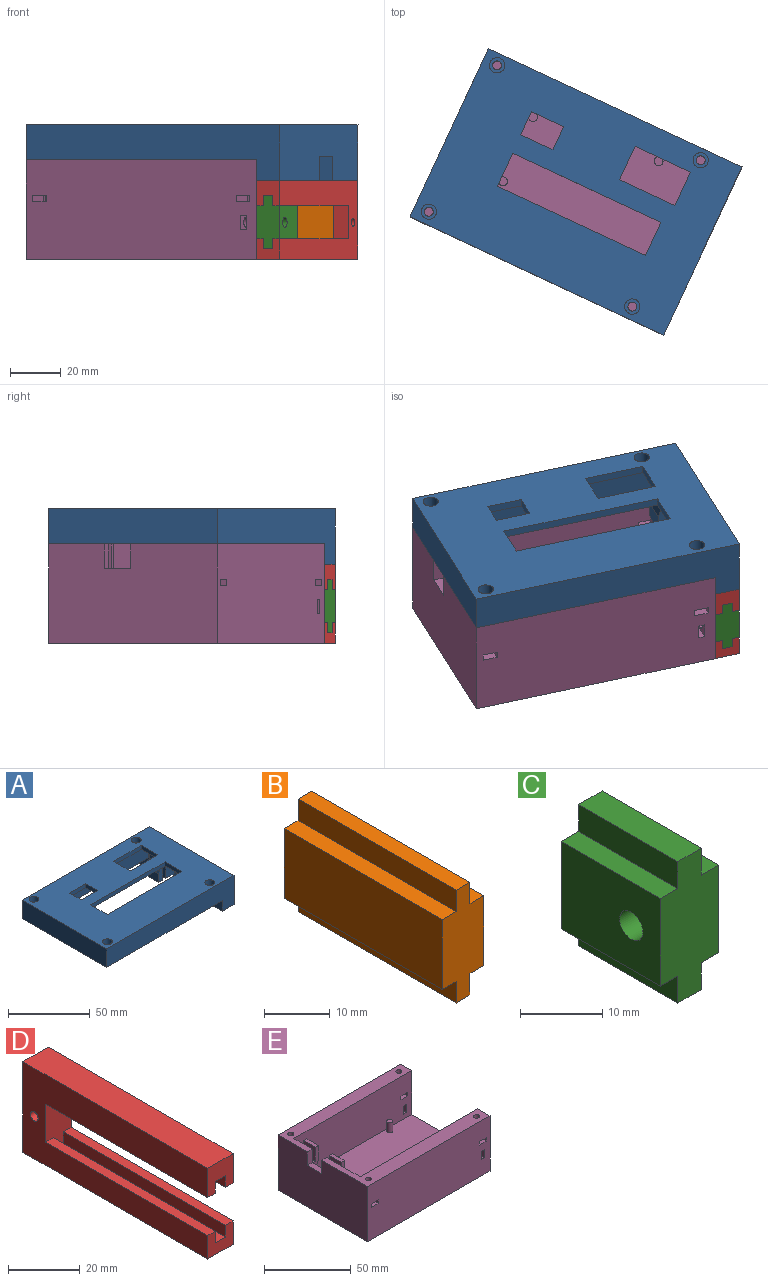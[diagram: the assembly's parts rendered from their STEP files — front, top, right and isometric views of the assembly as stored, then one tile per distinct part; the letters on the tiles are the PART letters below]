
ASSEMBLY  parts=5 mates=8
PART A: 56 faces, bbox 110x73x21.8 mm
  f0: plane 84x54mm, normal (0,0,-1), area 3044.5mm2, adj f1,f13,f14,f15,f25,f26,f27,f28
  f1: plane 73x18.8mm, normal (-1,0,0), area 881mm2, adj f0,f2,f8,f10,f12,f14,f15,f16
  f2: plane 37.4x10mm, normal (0,0,-1), area 374mm2, adj f1,f10,f11,f37
  f3: plane 110x73mm, normal (0,0,1), area 6505.4mm2, adj f9,f10,f11,f12,f18,f20,f22,f24
  f4: cylinder r=1.75mm len=8.8mm, axis (0,0,1), area 96.8mm2, adj f8,f23
  f5: cylinder r=1.75mm len=8.8mm, axis (0,0,1), area 96.8mm2, adj f8,f21
  f6: cylinder r=1.75mm len=8.8mm, axis (0,0,1), area 96.8mm2, adj f8,f19
  f7: cylinder r=1.75mm len=8.8mm, axis (0,0,1), area 96.8mm2, adj f8,f17
  f8: plane 100x73mm, normal (0,0,-1), area 2725.5mm2, adj f1,f4,f5,f6,f7,f9,f10,f12
  f9: plane 73x13.8mm, normal (-1,0,0), area 1007.4mm2, adj f3,f8,f10,f12
  f10: plane 110x21.8mm, normal (0,-1,0), area 1598mm2, adj f1,f2,f3,f8,f9,f11
  f11: plane 73x21.8mm, normal (1,0,0), area 1481.2mm2, adj f2,f3,f10,f12,f16,f37,f38,f39
  f12: plane 110x21.8mm, normal (0,1,0), area 1598mm2, adj f1,f3,f8,f9,f11,f16
  f13: plane 54x10.8mm, normal (1,0,0), area 583.2mm2, adj f0,f8,f14,f15
  f14: plane 84x10.8mm, normal (0,-1,0), area 907.2mm2, adj f0,f1,f8,f13
  f15: plane 84x10.8mm, normal (0,1,0), area 907.2mm2, adj f0,f1,f8,f13
  f16: plane 24x10mm, normal (0,0,-1), area 240mm2, adj f1,f11,f12,f38
  f17: plane 6x6mm, normal (0,0,1), area 18.7mm2, adj f7,f18
  f18: cylinder r=3mm len=6mm, axis (0,0,1), area 94.2mm2, adj f3,f17
  f19: plane 6x6mm, normal (0,0,1), area 18.7mm2, adj f6,f20
  f20: cylinder r=3mm len=6mm, axis (0,0,1), area 94.2mm2, adj f3,f19
  f21: plane 6x6mm, normal (0,0,1), area 18.7mm2, adj f5,f22
  f22: cylinder r=3mm len=6mm, axis (0,0,1), area 94.2mm2, adj f3,f21
  f23: plane 6x6mm, normal (0,0,1), area 18.7mm2, adj f4,f24
  f24: cylinder r=3mm len=6mm, axis (0,0,1), area 94.2mm2, adj f3,f23
  f25: plane 14x3mm, normal (0,-1,0), area 42mm2, adj f0,f3,f26,f28
  f26: plane 10x3mm, normal (1,0,0), area 30mm2, adj f0,f3,f25,f27
  f27: plane 14x3mm, normal (0,1,0), area 42mm2, adj f0,f3,f26,f28
  f28: plane 10x3mm, normal (-1,0,0), area 30mm2, adj f0,f3,f25,f27
  f29: plane 24x3mm, normal (0,-1,0), area 72mm2, adj f0,f3,f30,f32
  f30: plane 14.4x3mm, normal (1,0,0), area 43.2mm2, adj f0,f3,f29,f31
  f31: plane 24x3mm, normal (0,1,0), area 72mm2, adj f0,f3,f30,f32
  f32: plane 14.4x3mm, normal (-1,0,0), area 43.2mm2, adj f0,f3,f29,f31
  f33: plane 14.4x3mm, normal (1,0,0), area 43.2mm2, adj f0,f3,f34,f36
  f34: plane 64.3x3mm, normal (0,1,0), area 192.9mm2, adj f0,f3,f33,f35
  f35: plane 14.4x3mm, normal (-1,0,0), area 43.2mm2, adj f0,f3,f34,f36
  f36: plane 64.3x3mm, normal (0,-1,0), area 192.9mm2, adj f0,f3,f33,f35
  f37: plane 10x9.5mm, normal (0,1,0), area 95mm2, adj f1,f2,f11,f39
  f38: plane 10x9.5mm, normal (0,-1,0), area 95mm2, adj f1,f11,f16,f39
  f39: plane 11.6x10mm, normal (0,0,-1), area 116mm2, adj f1,f11,f37,f38
  f40: plane 10x10mm, normal (1,0,0), area 100mm2, adj f41,f45,f46,f47
  f41: plane 10x2.5mm, normal (0,0,-1), area 25mm2, adj f1,f40,f46,f47
  f42: plane 10x6.3mm, normal (-1,0,0), area 63mm2, adj f0,f43,f46,f47
  f43: plane 10x6.25mm, normal (-0.95,0,0.3), area 65.6mm2, adj f42,f44,f46,f47
  f44: plane 10x6.25mm, normal (-1,0,0), area 62.5mm2, adj f43,f45,f46,f47
  f45: plane 10x3.5mm, normal (0,0,-1), area 35mm2, adj f40,f44,f46,f47
  f46: plane 18.8x6mm, normal (0,1,0), area 68.9mm2, adj f0,f1,f40,f41,f42,f43,f44,f45
  f47: plane 18.8x6mm, normal (0,-1,0), area 68.9mm2, adj f0,f1,f40,f41,f42,f43,f44,f45
  f48: plane 10x10mm, normal (1,0,0), area 100mm2, adj f49,f53,f54,f55
  f49: plane 10x3.5mm, normal (0,0,-1), area 35mm2, adj f48,f50,f54,f55
  f50: plane 10x6.25mm, normal (-1,0,0), area 62.5mm2, adj f49,f51,f54,f55
  f51: plane 10x6.25mm, normal (-0.95,0,0.3), area 65.6mm2, adj f50,f52,f54,f55
  f52: plane 10x6.3mm, normal (-1,0,0), area 63mm2, adj f0,f51,f54,f55
  f53: plane 10x2.5mm, normal (0,0,-1), area 25mm2, adj f1,f48,f54,f55
  f54: plane 18.8x6mm, normal (0,-1,0), area 68.9mm2, adj f0,f1,f48,f49,f50,f51,f52,f53
  f55: plane 18.8x6mm, normal (0,1,0), area 68.9mm2, adj f0,f1,f48,f49,f50,f51,f52,f53
PART B: 14 faces, bbox 9x34x21 mm
  f0: plane 34x4mm, normal (1,0,0), area 136mm2, adj f1,f11,f12,f13
  f1: plane 34x3mm, normal (0,0,-1), area 102mm2, adj f0,f2,f12,f13
  f2: plane 34x13mm, normal (1,0,0), area 442mm2, adj f1,f3,f12,f13
  f3: plane 34x3mm, normal (0,0,1), area 102mm2, adj f2,f4,f12,f13
  f4: plane 34x4mm, normal (1,0,0), area 136mm2, adj f3,f5,f12,f13
  f5: plane 34x3mm, normal (0,0,1), area 102mm2, adj f4,f6,f12,f13
  f6: plane 34x4mm, normal (-1,0,0), area 136mm2, adj f5,f7,f12,f13
  f7: plane 34x3mm, normal (0,0,1), area 102mm2, adj f6,f8,f12,f13
  f8: plane 34x13mm, normal (-1,0,0), area 442mm2, adj f7,f9,f12,f13
  f9: plane 34x3mm, normal (0,0,-1), area 102mm2, adj f8,f10,f12,f13
  f10: plane 34x4mm, normal (-1,0,0), area 136mm2, adj f9,f11,f12,f13
  f11: plane 34x3mm, normal (0,0,-1), area 102mm2, adj f0,f10,f12,f13
  f12: plane 21x9mm, normal (0,1,0), area 141mm2, adj f0,f1,f2,f3,f4,f5,f6,f7
  f13: plane 21x9mm, normal (0,-1,0), area 141mm2, adj f0,f1,f2,f3,f4,f5,f6,f7
PART C: 15 faces, bbox 10x17x21 mm
  f0: plane 17x4mm, normal (1,0,0), area 68mm2, adj f1,f11,f12,f13
  f1: plane 17x3mm, normal (0,0,-1), area 51mm2, adj f0,f2,f12,f13
  f2: plane 17x13mm, normal (1,0,0), area 208.4mm2, adj f1,f3,f12,f13,f14
  f3: plane 17x3mm, normal (0,0,1), area 51mm2, adj f2,f4,f12,f13
  f4: plane 17x4mm, normal (1,0,0), area 68mm2, adj f3,f5,f12,f13
  f5: plane 17x4mm, normal (0,0,1), area 68mm2, adj f4,f6,f12,f13
  f6: plane 17x4mm, normal (-1,0,0), area 68mm2, adj f5,f7,f12,f13
  f7: plane 17x3mm, normal (0,0,1), area 51mm2, adj f6,f8,f12,f13
  f8: plane 17x13mm, normal (-1,0,0), area 208.4mm2, adj f7,f9,f12,f13,f14
  f9: plane 17x3mm, normal (0,0,-1), area 51mm2, adj f8,f10,f12,f13
  f10: plane 17x4mm, normal (-1,0,0), area 68mm2, adj f9,f11,f12,f13
  f11: plane 17x4mm, normal (0,0,-1), area 68mm2, adj f0,f10,f12,f13
  f12: plane 21x10mm, normal (0,-1,0), area 162mm2, adj f0,f1,f2,f3,f4,f5,f6,f7
  f13: plane 21x10mm, normal (0,1,0), area 162mm2, adj f0,f1,f2,f3,f4,f5,f6,f7
  f14: cylinder r=2mm len=10mm, axis (1,0,0), area 125.7mm2, adj f2,f8
PART D: 19 faces, bbox 10x73x31 mm
  f0: plane 10x10mm, normal (0,-1,0), area 84mm2, adj f1,f3,f4,f6,f9,f10,f11,f12
  f1: plane 73x31mm, normal (1,0,0), area 1423.9mm2, adj f0,f4,f5,f7,f8,f9,f16,f17
  f2: plane 64x3mm, normal (0,0,1), area 192mm2, adj f5,f6,f8,f13
  f3: plane 64x3mm, normal (0,0,-1), area 192mm2, adj f0,f6,f8,f10
  f4: plane 73x10mm, normal (0,0,1), area 730mm2, adj f0,f1,f6,f17
  f5: plane 10x8mm, normal (0,-1,0), area 64mm2, adj f1,f2,f6,f7,f13,f14,f15,f16
  f6: plane 73x31mm, normal (-1,0,0), area 1423.9mm2, adj f0,f2,f3,f4,f5,f8,f16,f17
  f7: plane 64x3mm, normal (0,0,1), area 192mm2, adj f1,f5,f8,f15
  f8: plane 21x10mm, normal (0,-1,0), area 162mm2, adj f1,f2,f3,f6,f7,f9,f10,f11
  f9: plane 64x3mm, normal (0,0,-1), area 192mm2, adj f0,f1,f8,f12
  f10: plane 64x4mm, normal (1,0,0), area 256mm2, adj f0,f3,f8,f11
  f11: plane 64x4mm, normal (0,0,-1), area 256mm2, adj f0,f8,f10,f12
  f12: plane 64x4mm, normal (-1,0,0), area 256mm2, adj f0,f8,f9,f11
  f13: plane 64x4mm, normal (1,0,0), area 256mm2, adj f2,f5,f8,f14
  f14: plane 64x4mm, normal (0,0,1), area 256mm2, adj f5,f8,f13,f15
  f15: plane 64x4mm, normal (-1,0,0), area 256mm2, adj f5,f7,f8,f14
  f16: plane 73x10mm, normal (0,0,-1), area 730mm2, adj f1,f5,f6,f17
  f17: plane 31x10mm, normal (0,1,0), area 310mm2, adj f1,f4,f6,f16
  f18: cylinder r=1.5mm len=10mm, axis (1,0,0), area 94.2mm2, adj f1,f6
PART E: 74 faces, bbox 100x73x39 mm
  f0: plane 100x39mm, normal (0,-1,0), area 3857.2mm2, adj f11,f12,f13,f14,f44,f45,f46,f47
  f1: plane 96x31mm, normal (0,1,0), area 2935.8mm2, adj f8,f9,f12,f13,f44,f46,f47,f49
  f2: plane 100x39mm, normal (0,1,0), area 3857.3mm2, adj f10,f11,f12,f14,f53,f54,f55,f56
  f3: plane 96x31mm, normal (0,-1,0), area 2935.8mm2, adj f8,f9,f10,f12,f53,f54,f55,f56
  f4: cylinder r=2mm len=4.42mm, axis (1,0,0), area 55.5mm2, adj f12,f71
  f5: cylinder r=2mm len=4.42mm, axis (1,0,0), area 55.5mm2, adj f12,f63
  f6: cylinder r=1.75mm len=13.81mm, axis (0,0,1), area 151.8mm2, adj f13,f49
  f7: cylinder r=1.75mm len=13.81mm, axis (0,0,1), area 151.8mm2, adj f13,f44
  f8: plane 96x54mm, normal (0,0,1), area 5107.5mm2, adj f1,f3,f9,f12,f18,f19,f20,f26
  f9: plane 54x31mm, normal (1,0,0), area 1158.6mm2, adj f1,f3,f8,f10,f13,f15,f16,f17
  f10: plane 100x24mm, normal (0,0,1), area 940.8mm2, adj f2,f3,f9,f11,f12,f15,f42,f43
  f11: plane 73x39mm, normal (-1,0,0), area 2736.8mm2, adj f0,f2,f10,f13,f14,f15,f16,f17
  f12: plane 73x39mm, normal (1,0,0), area 1147.9mm2, adj f0,f1,f2,f3,f4,f5,f8,f10
  f13: plane 100x37.4mm, normal (0,0,1), area 1090.4mm2, adj f0,f1,f6,f7,f9,f11,f12,f16
  f14: plane 100x73mm, normal (0,0,-1), area 7300mm2, adj f0,f2,f11,f12
  f15: plane 9.5x4mm, normal (0,-1,0), area 38mm2, adj f9,f10,f11,f17
  f16: plane 9.5x4mm, normal (0,1,0), area 38mm2, adj f9,f11,f13,f17
  f17: plane 11.6x4mm, normal (0,0,1), area 46.4mm2, adj f9,f11,f15,f16
  f18: plane 12.91x9.5mm, normal (1,0,0), area 122.6mm2, adj f8,f19,f20,f25
  f19: plane 31x5mm, normal (0,1,0), area 78.2mm2, adj f8,f9,f18,f21,f22,f23,f24,f25
  f20: plane 31x5mm, normal (0,-1,0), area 78.2mm2, adj f8,f9,f18,f21,f22,f23,f24,f25
  f21: plane 9.5x9.05mm, normal (1,0,0), area 85.9mm2, adj f19,f20,f22,f25
  f22: plane 9.5x2.5mm, normal (0,0,1), area 23.8mm2, adj f19,f20,f21,f23
  f23: plane 9.81x9.5mm, normal (-1,0,0), area 93.2mm2, adj f19,f20,f22,f24
  f24: plane 9.5x2.5mm, normal (0,0,1), area 23.7mm2, adj f9,f19,f20,f23
  f25: plane 9.5x9.05mm, normal (0.95,0,-0.31), area 90.5mm2, adj f18,f19,f20,f21
  f26: plane 12.91x9.5mm, normal (1,0,0), area 122.6mm2, adj f8,f27,f28,f30
  f27: plane 31x5mm, normal (0,-1,0), area 78.2mm2, adj f8,f9,f26,f29,f30,f31,f32,f33
  f28: plane 31x5mm, normal (0,1,0), area 78.2mm2, adj f8,f9,f26,f29,f30,f31,f32,f33
  f29: plane 9.5x9.05mm, normal (1,0,0), area 85.9mm2, adj f27,f28,f30,f33
  f30: plane 9.5x9.05mm, normal (0.95,0,-0.31), area 90.5mm2, adj f26,f27,f28,f29
  f31: plane 9.5x2.5mm, normal (0,0,1), area 23.8mm2, adj f9,f27,f28,f32
  f32: plane 9.81x9.5mm, normal (-1,0,0), area 93.2mm2, adj f27,f28,f31,f33
  f33: plane 9.5x2.5mm, normal (0,0,1), area 23.8mm2, adj f27,f28,f29,f32
  f34: cylinder r=1.75mm len=7mm, axis (0,0,-1), area 77mm2, adj f8,f35
  f35: plane 3.5x3.5mm, normal (0,0,1), area 9.6mm2, adj f34
  f36: cylinder r=1.75mm len=7mm, axis (0,0,-1), area 77mm2, adj f8,f37
  f37: plane 3.5x3.5mm, normal (0,0,1), area 9.6mm2, adj f36
  f38: cylinder r=1.75mm len=7mm, axis (0,0,-1), area 77mm2, adj f8,f39
  f39: plane 3.5x3.5mm, normal (0,0,1), area 9.6mm2, adj f38
  f40: cylinder r=1.75mm len=7mm, axis (0,0,-1), area 77mm2, adj f8,f41
  f41: plane 3.5x3.5mm, normal (0,0,1), area 9.6mm2, adj f40
  f42: cylinder r=1.75mm len=13.81mm, axis (0,0,1), area 151.8mm2, adj f10,f57
  f43: cylinder r=1.75mm len=13.81mm, axis (0,0,1), area 151.8mm2, adj f10,f53
  f44: plane 10x5.7mm, normal (0,0,-1), area 47.4mm2, adj f0,f1,f7,f45,f47,f48
  f45: plane 10x2.5mm, normal (1,0,0), area 25mm2, adj f0,f44,f46,f48
  f46: plane 10x5.7mm, normal (0,0,1), area 57mm2, adj f0,f1,f45,f47,f48
  f47: plane 10x2.5mm, normal (-1,0,0), area 25mm2, adj f0,f1,f44,f46
  f48: plane 2.5x1mm, normal (0,-1,0), area 2.5mm2, adj f9,f44,f45,f46
  f49: plane 10x5.7mm, normal (0,0,-1), area 47.4mm2, adj f0,f1,f6,f50,f52
  f50: plane 10x2.5mm, normal (1,0,0), area 25mm2, adj f0,f1,f49,f51
  f51: plane 10x5.7mm, normal (0,0,1), area 57mm2, adj f0,f1,f50,f52
  f52: plane 10x2.5mm, normal (-1,0,0), area 25mm2, adj f0,f1,f49,f51
  f53: plane 9x5.7mm, normal (0,0,-1), area 41.7mm2, adj f2,f3,f43,f54,f56
  f54: plane 9x2.5mm, normal (-1,0,0), area 22.5mm2, adj f2,f3,f53,f55
  f55: plane 9x5.7mm, normal (0,0,1), area 51.3mm2, adj f2,f3,f54,f56
  f56: plane 9x2.5mm, normal (1,0,0), area 22.5mm2, adj f2,f3,f53,f55
  f57: plane 10x5.7mm, normal (0,0,-1), area 42.7mm2, adj f2,f3,f9,f42,f58,f60,f61
  f58: plane 9x2.5mm, normal (-1,0,0), area 22.5mm2, adj f2,f3,f57,f59
  f59: plane 10x5.7mm, normal (0,0,1), area 52.3mm2, adj f2,f3,f9,f58,f60,f61
  f60: plane 10x2.5mm, normal (1,0,0), area 25mm2, adj f2,f57,f59,f61
  f61: plane 2.5x1mm, normal (0,1,0), area 2.5mm2, adj f9,f57,f59,f60
  f62: plane 9x5.7mm, normal (1,0,0), area 38.7mm2, adj f2,f3,f64,f65,f67
  f63: plane 9x5.7mm, normal (-1,0,0), area 38.7mm2, adj f2,f3,f5,f64,f65
  f64: plane 9x2.5mm, normal (0,0,1), area 22.5mm2, adj f2,f3,f62,f63
  f65: plane 9x2.5mm, normal (0,0,-1), area 22.5mm2, adj f2,f3,f62,f63
  f66: plane 4x4mm, normal (1,0,0), area 12.6mm2, adj f67
  f67: cylinder r=2mm len=4mm, axis (1,0,0), area 38.8mm2, adj f62,f66
  f68: plane 10x2.5mm, normal (0,0,-1), area 25mm2, adj f0,f1,f70,f71
  f69: plane 10x2.5mm, normal (0,0,1), area 25mm2, adj f0,f1,f70,f71
  f70: plane 10x5.7mm, normal (1,0,0), area 44.4mm2, adj f0,f1,f68,f69,f73
  f71: plane 10x5.7mm, normal (-1,0,0), area 44.4mm2, adj f0,f1,f4,f68,f69
  f72: plane 4x4mm, normal (1,0,0), area 12.6mm2, adj f73
  f73: cylinder r=2mm len=4mm, axis (1,0,0), area 38.8mm2, adj f70,f72
PLACE A rot(axis=(0,0,-1),25deg) t=(-47.46,21.27,61.82)mm
PLACE B rot(axis=(0.98,-0.22,0),180deg) t=(53.53,-7.06,47.82)mm
PLACE C rot(axis=(0,0,-1),25deg) t=(53.08,-6.85,26.82)mm
PLACE D rot(axis=(0,0,-1),25deg) t=(43.17,-20.99,25.82)mm
PLACE E rot(axis=(0,0,-1),25deg) t=(-47.46,21.27,22.82)mm fixed
MATE planar E.f14 <-> D.f16  axis (0,0,-1) through (13.28,33.22,22.82)mm
MATE slider B.f13 <-> C.f13  axis (0.42,0.91,0) through (69.26,23.12,37.32)mm
MATE planar A.f10 <-> E.f0  axis (-0.42,-0.91,0) through (4.66,-3.03,68.18)mm
MATE planar B.f3 <-> D.f7  axis (0,0,-1) through (64.79,6.44,30.82)mm
MATE revolute E.f5 <-> D.f18  axis (0.91,-0.42,0) through (72.12,41.09,37.32)mm
MATE planar A.f9 <-> E.f11  axis (-0.91,0.42,0) through (-32.03,54.35,68.72)mm
MATE planar A.f16 <-> D.f4  axis (0,0,-1) through (73.49,32.18,53.82)mm
MATE revolute E.f4 <-> C.f14  axis (0.91,-0.42,0) through (45.29,-16.46,37.32)mm
